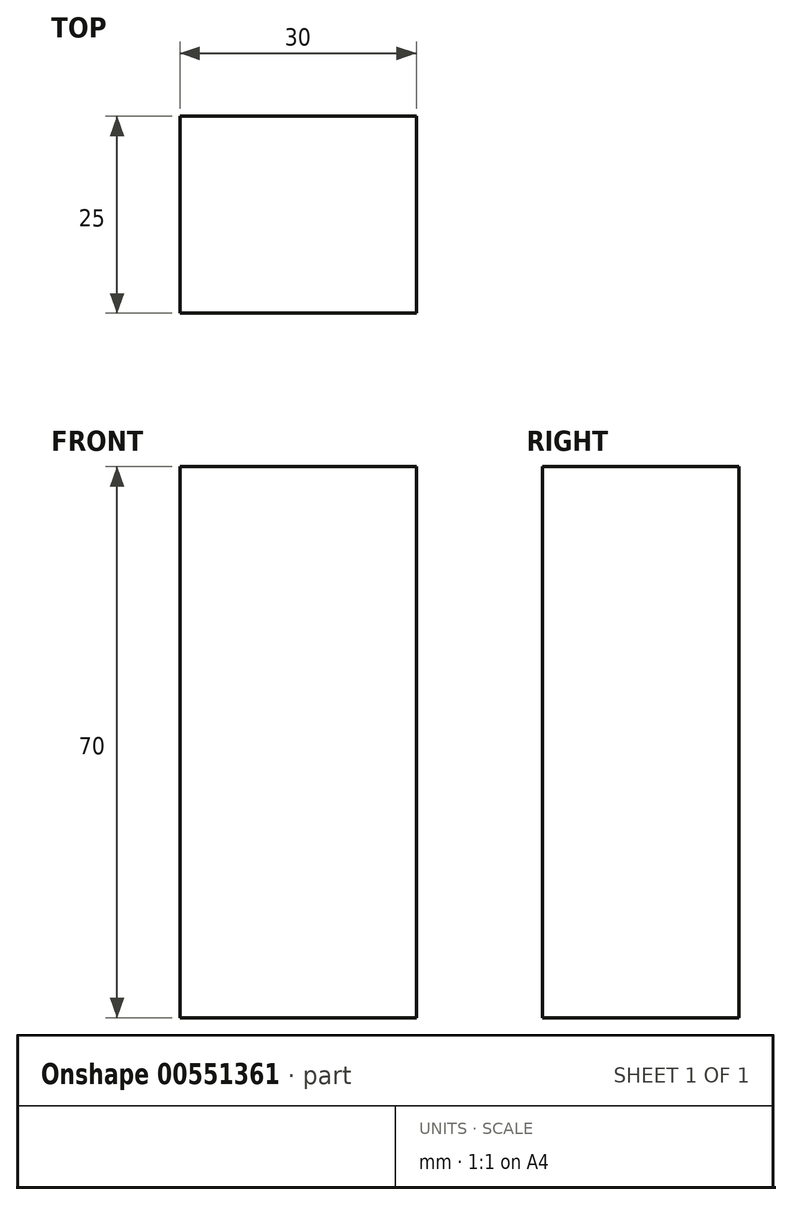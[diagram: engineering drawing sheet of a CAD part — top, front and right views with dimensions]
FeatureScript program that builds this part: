
annotation { "Feature Type Name" : "Feature", "Feature Type Description" : "" }
export const myFeature = defineFeature(function(context is Context, id is Id, definition is map)
    precondition{}
    {
        {
            var Q0;
            Q0=qCreatedBy(makeId("Front.planeOp"),FACE);
            var sketch = newSketch(context, id + "F0", { "sketchPlane" : qUnion([Q0])});
            skLineSegment(sketch, "E0.bottom", {"start": v(-27.68, 28.34) * mm, "end": v(2.32, 28.34) * mm});
            skLineSegment(sketch, "E0.top", {"start": v(-27.68, -41.66) * mm, "end": v(2.32, -41.66) * mm});
            skLineSegment(sketch, "E0.left", {"start": v(-27.68, 28.34) * mm, "end": v(-27.68, -41.66) * mm});
            skLineSegment(sketch, "E0.right", {"start": v(2.32, 28.34) * mm, "end": v(2.32, -41.66) * mm});
            skLineSegment(sketch, "E1.bottom", {"start": v(-22.06, -41.66) * mm, "end": v(-4.88, -41.66) * mm});
            skLineSegment(sketch, "E1.top", {"start": v(-22.06, 18.8) * mm, "end": v(-4.88, 18.8) * mm});
            skLineSegment(sketch, "E1.left", {"start": v(-22.06, -41.66) * mm, "end": v(-22.06, 18.8) * mm});
            skLineSegment(sketch, "E1.right", {"start": v(-4.88, -41.66) * mm, "end": v(-4.88, 18.8) * mm});
            skSolve(sketch);
        }
        {
            var Q0;
            Q0 = qSketchRegion(id + "F0", true);
            extrude(context, id + "F1", {"entities" : qUnion([Q0]), "depth" : 25 * mm, "offsetDistance" : 25 * mm});
        }
    });
